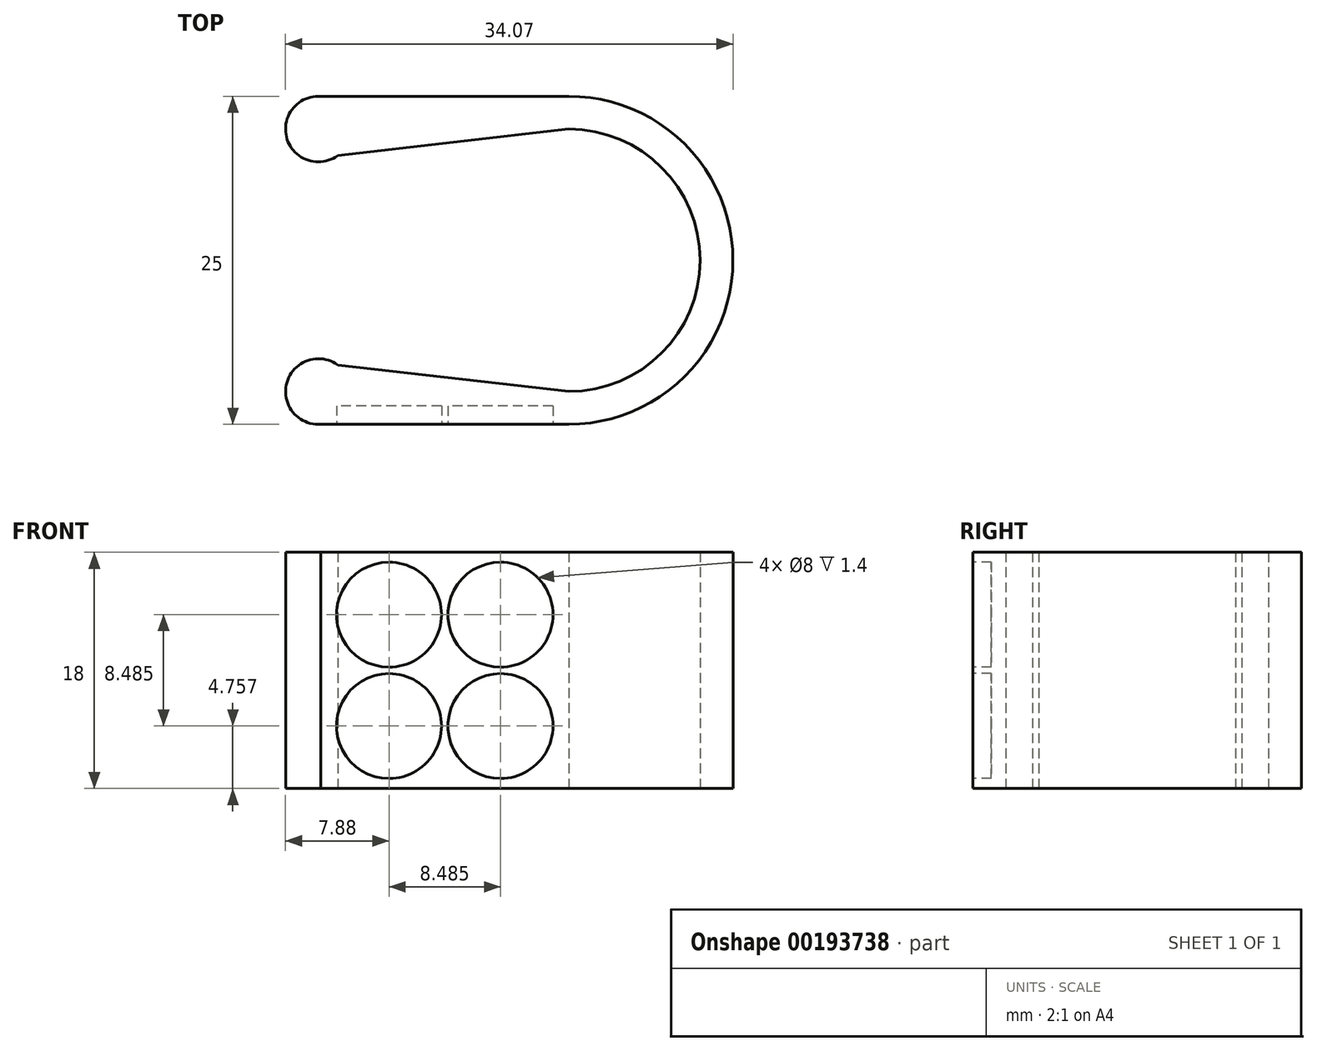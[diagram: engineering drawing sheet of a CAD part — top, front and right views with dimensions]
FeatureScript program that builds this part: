
annotation { "Feature Type Name" : "Feature", "Feature Type Description" : "" }
export const myFeature = defineFeature(function(context is Context, id is Id, definition is map)
    precondition{}
    {
        {
            var Q0;
            Q0=qCreatedBy(makeId("Top.planeOp"),FACE);
            var sketch = newSketch(context, id + "F0", { "sketchPlane" : qUnion([Q0])});
            skArc(sketch, "E0", {"start": v(0, -10) * mm, "mid": v(10, 0) * mm, "end": v(0, 10) * mm});
            skArc(sketch, "E1", {"start": v(0, -12.5) * mm, "mid": v(12.5, 0) * mm, "end": v(0, 12.5) * mm});
            skLineSegment(sketch, "E2", {"start": v(-19.07, 10) * mm, "end": v(-19.07, -10) * mm, "construction": true});
            skLineSegment(sketch, "E3", {"start": v(-17.6, 7.98) * mm, "end": v(0, 10) * mm});
            skLineSegment(sketch, "E4", {"start": v(0, -10) * mm, "end": v(-17.6, -7.98) * mm});
            skCircle(sketch, "E5", {"center": v(-19.07, 10) * mm, "radius": 2.5 * mm});
            skCircle(sketch, "E6", {"center": v(-19.07, -10) * mm, "radius": 2.5 * mm});
            skLineSegment(sketch, "E7", {"start": v(0, 12.5) * mm, "end": v(-19.07, 12.5) * mm});
            skLineSegment(sketch, "E8", {"start": v(0, -12.5) * mm, "end": v(-18.9, -12.5) * mm});
            skSolve(sketch);
        }
        {
            var Q0;
            Q0 = qSketchRegion(id + "F0", true);
            extrude(context, id + "F1", {"entities" : qUnion([Q0]), "depth" : 18 * mm, "offsetDistance" : 25 * mm});
        }
        {
            var Q0;
            Q0=makeQuery(id+"F1.opExtrude","SWEPT_FACE",FACE,{"disambiguationData":[OSD([sQuery(id+"F0.wireOp",EDGE,"E8")])]});
            var sketch = newSketch(context, id + "F2", { "sketchPlane" : qUnion([Q0])});
            skCircle(sketch, "E9", {"center": v(-13.69, 4.76) * mm, "radius": 4 * mm});
            skCircle(sketch, "E10", {"center": v(-13.69, 13.24) * mm, "radius": 4 * mm});
            skCircle(sketch, "E11", {"center": v(-5.2, 13.24) * mm, "radius": 4 * mm});
            skCircle(sketch, "E12", {"center": v(-5.2, 4.76) * mm, "radius": 4 * mm});
            skLineSegment(sketch, "E13", {"start": v(-5.2, 4.76) * mm, "end": v(-13.69, 13.24) * mm, "construction": true});
            skLineSegment(sketch, "E14", {"start": v(-5.2, 13.24) * mm, "end": v(-13.69, 4.76) * mm, "construction": true});
            skLineSegment(sketch, "E15", {"start": v(0, 0) * mm, "end": v(-18.89, 18) * mm, "construction": true});
            skLineSegment(sketch, "E16", {"start": v(0, 18) * mm, "end": v(-18.89, 0) * mm, "construction": true});
            skPoint(sketch, "E17", {"position": v(-9.44, 9) * mm});
            skSolve(sketch);
        }
        {
            var Q0;
            Q0 = qSketchRegion(id + "F2", true);
            extrude(context, id + "F3", {"entities" : qUnion([Q0]), "operationType" : NewBodyOperationType.REMOVE, "oppositeDirection" : true, "depth" : 1.4 * mm, "offsetDistance" : 25 * mm});
        }
    });
